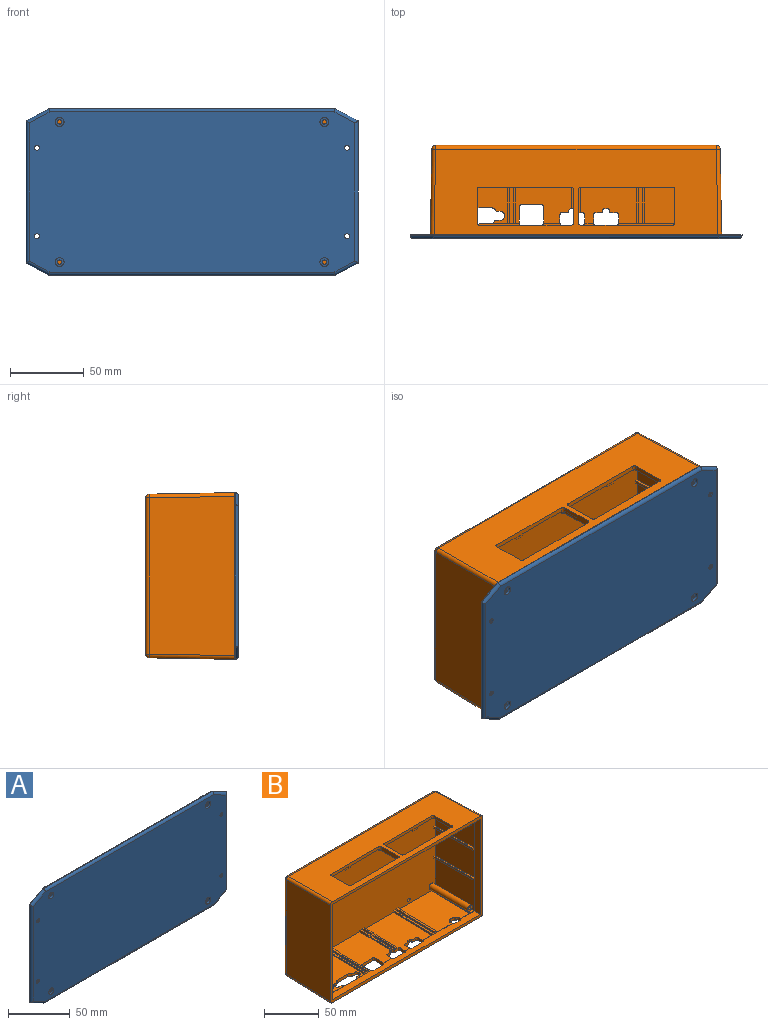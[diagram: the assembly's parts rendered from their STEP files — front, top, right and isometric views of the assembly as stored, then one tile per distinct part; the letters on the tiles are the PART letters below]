
ASSEMBLY  parts=2 mates=1
PART A: 84 faces, bbox 225x7.3x113 mm
  f0: cylinder r=3mm len=6mm, axis (0,-1,0), area 39.6mm2, adj f35,f83
  f1: cylinder r=1.45mm len=3.16mm, axis (0,-1,0), area 28.8mm2, adj f78,f83
  f2: cylinder r=3mm len=6mm, axis (0,-1,0), area 39.6mm2, adj f35,f82
  f3: cylinder r=1.45mm len=3.16mm, axis (0,-1,0), area 28.8mm2, adj f79,f82
  f4: cylinder r=3mm len=6mm, axis (0,-1,0), area 39.6mm2, adj f35,f81
  f5: cylinder r=1.45mm len=3.16mm, axis (0,-1,0), area 28.8mm2, adj f76,f81
  f6: cylinder r=3mm len=6mm, axis (0,-1,0), area 39.6mm2, adj f35,f80
  f7: cylinder r=1.45mm len=3.16mm, axis (0,-1,0), area 28.8mm2, adj f77,f80
  f8: cone r=3.15mm half-angle=45deg, axis (0,1,0), area 31.2mm2, adj f9,f26
  f9: cylinder r=1.7mm len=3.4mm, axis (0,1,0), area 11.6mm2, adj f8,f35
  f10: cone r=3.15mm half-angle=45deg, axis (0,1,0), area 31.2mm2, adj f11,f26
  f11: cylinder r=1.7mm len=3.4mm, axis (0,1,0), area 11.6mm2, adj f10,f35
  f12: cone r=3.15mm half-angle=45deg, axis (0,1,0), area 31.2mm2, adj f13,f26
  f13: cylinder r=1.7mm len=3.4mm, axis (0,1,0), area 11.6mm2, adj f12,f35
  f14: cone r=3.15mm half-angle=45deg, axis (0,1,0), area 31.2mm2, adj f15,f26
  f15: cylinder r=1.7mm len=3.4mm, axis (0,1,0), area 11.6mm2, adj f14,f35
  f16: cylinder r=3.17mm len=6.35mm, axis (0,1,0), area 40.5mm2, adj f44,f79
  f17: cylinder r=3.17mm len=6.35mm, axis (0,1,0), area 40.5mm2, adj f45,f78
  f18: cylinder r=3.17mm len=6.35mm, axis (0,1,0), area 40.5mm2, adj f46,f77
  f19: cylinder r=3.17mm len=6.35mm, axis (0,1,0), area 40.5mm2, adj f47,f76
  f20: cylinder r=0.76mm len=1.52mm, axis (0,-1,0), area 3mm2, adj f26,f67,f69,f70
  f21: cylinder r=0.76mm len=1.52mm, axis (0,-1,0), area 3mm2, adj f26,f58,f60,f61
  f22: cylinder r=4.92mm len=9.84mm, axis (0,-1,0), area 146.9mm2, adj f26,f47
  f23: cylinder r=4.92mm len=9.84mm, axis (0,-1,0), area 146.9mm2, adj f26,f46
  f24: cylinder r=4.92mm len=9.84mm, axis (0,-1,0), area 146.9mm2, adj f26,f45
  f25: cylinder r=4.92mm len=9.84mm, axis (0,-1,0), area 146.9mm2, adj f26,f44
  f26: plane 225.04x113.03mm, normal (0,1,0), area 24179.3mm2, adj f8,f10,f12,f14,f20,f21,f22,f23
  f27: plane 15.75x8.26mm, normal (0.46,0,-0.89), area 5.6mm2, adj f26,f28,f34,f41
  f28: plane 193.55x0.32mm, normal (0,0,-1), area 61.5mm2, adj f26,f27,f29,f43
  f29: plane 15.75x8.26mm, normal (-0.46,0,-0.89), area 5.6mm2, adj f26,f28,f30,f42
  f30: plane 96.52x0.32mm, normal (-1,0,0), area 30.6mm2, adj f26,f29,f31,f40
  f31: plane 15.75x8.26mm, normal (-0.46,0,0.89), area 5.6mm2, adj f26,f30,f32,f38
  f32: plane 193.55x0.32mm, normal (0,0,1), area 61.5mm2, adj f26,f31,f33,f36
  f33: plane 15.75x8.26mm, normal (0.46,0,0.89), area 5.6mm2, adj f26,f32,f34,f37
  f34: plane 96.52x0.32mm, normal (1,0,0), area 30.6mm2, adj f26,f27,f33,f39
  f35: plane 220.6x108.59mm, normal (0,-1,0), area 23596.7mm2, adj f0,f2,f4,f6,f9,f11,f13,f15
  f36: cylinder r=2.22mm len=193.55mm, axis (-1,0,0), area 674.3mm2, adj f32,f35,f37,f38
  f37: cylinder r=2.22mm len=16.78mm, axis (-0.89,0,0.46), area 59.7mm2, adj f33,f35,f36,f39
  f38: cylinder r=2.22mm len=16.78mm, axis (-0.89,0,-0.46), area 59.7mm2, adj f31,f35,f36,f40
  f39: cylinder r=2.22mm len=96.52mm, axis (0,0,1), area 333.5mm2, adj f34,f35,f37,f41
  f40: cylinder r=2.22mm len=96.52mm, axis (0,0,-1), area 333.5mm2, adj f30,f35,f38,f42
  f41: cylinder r=2.22mm len=16.78mm, axis (0.89,0,0.46), area 59.7mm2, adj f27,f35,f39,f43
  f42: cylinder r=2.22mm len=16.78mm, axis (0.89,0,-0.46), area 59.7mm2, adj f29,f35,f40,f43
  f43: cylinder r=2.22mm len=193.55mm, axis (1,0,0), area 674.3mm2, adj f28,f35,f41,f42
  f44: plane 9.84x9.84mm, normal (0,1,0), area 44.4mm2, adj f16,f25
  f45: plane 9.84x9.84mm, normal (0,1,0), area 44.4mm2, adj f17,f24
  f46: plane 9.84x9.84mm, normal (0,1,0), area 44.4mm2, adj f18,f23
  f47: plane 9.84x9.84mm, normal (0,1,0), area 44.4mm2, adj f19,f22
  f48: cylinder r=0.76mm len=1.52mm, axis (0,-1,0), area 3mm2, adj f26,f49,f51,f52
  f49: plane 60.96x1.27mm, normal (0,0,1), area 77.4mm2, adj f26,f48,f50,f52
  f50: cylinder r=0.76mm len=1.52mm, axis (0,-1,0), area 3mm2, adj f26,f49,f51,f52
  f51: plane 60.96x1.27mm, normal (0,0,-1), area 77.4mm2, adj f26,f48,f50,f52
  f52: plane 62.48x1.52mm, normal (0,1,0), area 94.7mm2, adj f48,f49,f50,f51
  f53: cylinder r=0.76mm len=1.52mm, axis (0,-1,0), area 3mm2, adj f26,f54,f56,f57
  f54: plane 60.96x1.27mm, normal (0,0,1), area 77.4mm2, adj f26,f53,f55,f57
  f55: cylinder r=0.76mm len=1.52mm, axis (0,-1,0), area 3mm2, adj f26,f54,f56,f57
  f56: plane 60.96x1.27mm, normal (0,0,-1), area 77.4mm2, adj f26,f53,f55,f57
  f57: plane 62.48x1.52mm, normal (0,1,0), area 94.7mm2, adj f53,f54,f55,f56
  f58: plane 60.96x1.27mm, normal (-1,0,0), area 77.4mm2, adj f21,f26,f59,f61
  f59: cylinder r=0.76mm len=1.52mm, axis (0,-1,0), area 3mm2, adj f26,f58,f60,f61
  f60: plane 60.96x1.27mm, normal (1,0,0), area 77.4mm2, adj f21,f26,f59,f61
  f61: plane 62.48x1.52mm, normal (0,1,0), area 94.7mm2, adj f21,f58,f59,f60
  f62: cylinder r=0.76mm len=1.52mm, axis (0,-1,0), area 3mm2, adj f26,f63,f65,f66
  f63: plane 60.96x1.27mm, normal (0,0,-1), area 77.4mm2, adj f26,f62,f64,f66
  f64: cylinder r=0.76mm len=1.52mm, axis (0,-1,0), area 3mm2, adj f26,f63,f65,f66
  f65: plane 60.96x1.27mm, normal (0,0,1), area 77.4mm2, adj f26,f62,f64,f66
  f66: plane 62.48x1.52mm, normal (0,1,0), area 94.7mm2, adj f62,f63,f64,f65
  f67: plane 60.96x1.27mm, normal (-1,0,0), area 77.4mm2, adj f20,f26,f68,f70
  f68: cylinder r=0.76mm len=1.52mm, axis (0,-1,0), area 3mm2, adj f26,f67,f69,f70
  f69: plane 60.96x1.27mm, normal (1,0,0), area 77.4mm2, adj f20,f26,f68,f70
  f70: plane 62.48x1.52mm, normal (0,1,0), area 94.7mm2, adj f20,f67,f68,f69
  f71: cylinder r=0.76mm len=1.52mm, axis (0,-1,0), area 3mm2, adj f26,f72,f74,f75
  f72: plane 60.96x1.27mm, normal (0,0,-1), area 77.4mm2, adj f26,f71,f73,f75
  f73: cylinder r=0.76mm len=1.52mm, axis (0,-1,0), area 3mm2, adj f26,f72,f74,f75
  f74: plane 60.96x1.27mm, normal (0,0,1), area 77.4mm2, adj f26,f71,f73,f75
  f75: plane 62.48x1.52mm, normal (0,1,0), area 94.7mm2, adj f71,f72,f73,f74
  f76: plane 6.35x6.35mm, normal (0,1,0), area 25.1mm2, adj f5,f19
  f77: plane 6.35x6.35mm, normal (0,1,0), area 25.1mm2, adj f7,f18
  f78: plane 6.35x6.35mm, normal (0,1,0), area 25.1mm2, adj f1,f17
  f79: plane 6.35x6.35mm, normal (0,1,0), area 25.1mm2, adj f3,f16
  f80: plane 6x6mm, normal (0,-1,0), area 21.7mm2, adj f6,f7
  f81: plane 6x6mm, normal (0,-1,0), area 21.7mm2, adj f4,f5
  f82: plane 6x6mm, normal (0,-1,0), area 21.7mm2, adj f2,f3
  f83: plane 6x6mm, normal (0,-1,0), area 21.7mm2, adj f0,f1
PART B: 273 faces, bbox 197.4x60.5x113 mm
  f0: cylinder r=1.65mm len=3.3mm, axis (0,1,0), area 32.9mm2, adj f96,f111
  f1: cylinder r=1.38mm len=49.53mm, axis (0,1,0), area 430.8mm2, adj f193,f197
  f2: cylinder r=1.38mm len=49.53mm, axis (0,1,0), area 430.8mm2, adj f193,f196
  f3: cylinder r=1.38mm len=49.53mm, axis (0,1,0), area 430.8mm2, adj f192,f195
  f4: cylinder r=1.38mm len=49.53mm, axis (0,1,0), area 430.8mm2, adj f192,f194
  f5: cylinder r=3.17mm len=6.35mm, axis (0,0,1), area 31.7mm2, adj f18,f59,f184,f185
  f6: torus R=2.09mm, axis (0,-1,0), area 5.6mm2, adj f111,f112
  f7: torus R=2.09mm, axis (0,-1,0), area 6.5mm2, adj f96,f110
  f8: cylinder r=3.17mm len=49.53mm, axis (0,1,0), area 956.6mm2, adj f84,f85,f111,f149,f192
  f9: cylinder r=3.17mm len=49.53mm, axis (0,1,0), area 956.6mm2, adj f86,f87,f111,f150,f193
  f10: cylinder r=3.17mm len=49.53mm, axis (0,1,0), area 956.6mm2, adj f80,f81,f111,f117,f192
  f11: cylinder r=3.17mm len=49.53mm, axis (0,1,0), area 956.6mm2, adj f82,f83,f111,f118,f193
  f12: plane 49.53x5.33mm, normal (0,-0.02,1), area 242.4mm2, adj f39,f86,f111,f193
  f13: plane 49.53x42.76mm, normal (0,-0.02,1), area 2062.1mm2, adj f34,f87,f111,f193,f230,f231,f233,f234
  f14: plane 49.53x2.16mm, normal (0,-0.02,1), area 107mm2, adj f33,f37,f111,f269
  f15: plane 49.53x37.72mm, normal (0,-0.02,1), area 1712mm2, adj f36,f93,f111,f226,f229,f238,f239,f241
  f16: plane 49.53x37.72mm, normal (0,-0.02,1), area 1596.8mm2, adj f28,f91,f111,f199,f200,f201,f218,f219
  f17: plane 49.53x2.16mm, normal (0,-0.02,1), area 107mm2, adj f27,f31,f111,f270
  f18: plane 49.53x42.76mm, normal (0,-0.02,1), area 1855.7mm2, adj f5,f30,f84,f111,f181,f182,f183,f184
  f19: plane 49.53x5.33mm, normal (0,-0.02,1), area 242.4mm2, adj f42,f85,f111,f192
  f20: plane 49.53x5.33mm, normal (0,-0.02,-1), area 242.4mm2, adj f41,f82,f111,f193
  f21: plane 49.53x42.76mm, normal (0,-0.02,-1), area 1625.2mm2, adj f75,f83,f111,f193,f202,f203,f215,f216
  f22: plane 49.53x2.16mm, normal (0,-0.02,-1), area 107mm2, adj f57,f58,f111,f266
  f23: plane 49.53x42.76mm, normal (0,-0.02,-1), area 1625.2mm2, adj f73,f80,f111,f192,f206,f209,f212,f213
  f24: plane 49.53x5.33mm, normal (0,-0.02,-1), area 242.4mm2, adj f44,f81,f111,f192
  f25: plane 33.87x1.91mm, normal (0,-0.02,-1), area 34.6mm2, adj f57,f70,f145,f207,f210,f211,f266
  f26: plane 33.87x1.91mm, normal (0,-0.02,-1), area 34.6mm2, adj f58,f79,f146,f204,f214,f217,f266
  f27: plane 49.53x2.85mm, normal (-1,0,0), area 81.6mm2, adj f17,f29,f152,f159,f160,f173,f175,f270
  f28: plane 49.53x2.85mm, normal (1,0,0), area 81.6mm2, adj f16,f29,f152,f159,f160,f173,f175,f270
  f29: plane 33.87x1.91mm, normal (0,-0.02,1), area 64.5mm2, adj f27,f28,f175,f270
  f30: plane 49.53x2.85mm, normal (-1,0,0), area 81.6mm2, adj f18,f32,f153,f157,f158,f174,f176,f270
  f31: plane 49.53x2.85mm, normal (1,0,0), area 81.6mm2, adj f17,f32,f153,f157,f158,f174,f176,f270
  f32: plane 33.87x1.91mm, normal (0,-0.02,1), area 64.5mm2, adj f30,f31,f176,f270
  f33: plane 49.53x2.85mm, normal (-1,0,0), area 81.6mm2, adj f14,f35,f154,f167,f168,f169,f180,f269
  f34: plane 49.53x2.85mm, normal (1,0,0), area 81.6mm2, adj f13,f35,f154,f167,f168,f169,f180,f269
  f35: plane 33.87x1.91mm, normal (0,-0.02,1), area 64.5mm2, adj f33,f34,f180,f269
  f36: plane 49.53x2.85mm, normal (-1,0,0), area 81.6mm2, adj f15,f38,f155,f165,f166,f170,f179,f269
  f37: plane 49.53x2.85mm, normal (1,0,0), area 81.6mm2, adj f14,f38,f155,f165,f166,f170,f179,f269
  f38: plane 33.87x1.91mm, normal (0,-0.02,1), area 64.5mm2, adj f36,f37,f179,f269
  f39: plane 49.53x35.58mm, normal (-1,-0.02,0), area 1740.9mm2, adj f12,f51,f111,f193
  f40: plane 49.53x31.42mm, normal (-1,-0.02,0), area 1556.5mm2, adj f52,f54,f111,f193
  f41: plane 49.53x35.58mm, normal (-1,-0.02,0), area 1740.9mm2, adj f20,f55,f111,f193
  f42: plane 49.53x35.58mm, normal (1,-0.02,0), area 1740.9mm2, adj f19,f46,f111,f192
  f43: plane 49.53x31.42mm, normal (1,-0.02,0), area 1556.5mm2, adj f45,f49,f111,f192
  f44: plane 49.53x35.58mm, normal (1,-0.02,0), area 1740.9mm2, adj f24,f48,f111,f192
  f45: plane 49.53x2.45mm, normal (0,0,1), area 78.6mm2, adj f43,f47,f113,f192
  f46: plane 49.53x2.45mm, normal (0,0,-1), area 78.6mm2, adj f42,f47,f113,f192
  f47: plane 49.5x1.91mm, normal (1,-0.02,0), area 94.3mm2, adj f45,f46,f113,f192
  f48: plane 49.53x2.45mm, normal (0,0,1), area 78.6mm2, adj f44,f50,f114,f192
  f49: plane 49.53x2.45mm, normal (0,0,-1), area 78.6mm2, adj f43,f50,f114,f192
  f50: plane 49.5x1.91mm, normal (1,-0.02,0), area 94.3mm2, adj f48,f49,f114,f192
  f51: plane 49.53x2.45mm, normal (0,0,-1), area 78.6mm2, adj f39,f53,f115,f193
  f52: plane 49.53x2.45mm, normal (0,0,1), area 78.6mm2, adj f40,f53,f115,f193
  f53: plane 49.5x1.91mm, normal (-1,-0.02,0), area 94.3mm2, adj f51,f52,f115,f193
  f54: plane 49.53x2.45mm, normal (0,0,-1), area 78.6mm2, adj f40,f56,f116,f193
  f55: plane 49.53x2.45mm, normal (0,0,1), area 78.6mm2, adj f41,f56,f116,f193
  f56: plane 49.5x1.91mm, normal (-1,-0.02,0), area 94.3mm2, adj f54,f55,f116,f193
  f57: plane 49.53x2.85mm, normal (1,0,0), area 81.6mm2, adj f22,f25,f119,f129,f130,f140,f145,f266
  f58: plane 49.53x2.85mm, normal (-1,0,0), area 81.6mm2, adj f22,f26,f124,f131,f132,f139,f146,f266
  f59: plane 192.33x57.98mm, normal (0,0.02,-1), area 10210.2mm2, adj f5,f97,f99,f105,f106,f181,f182,f183
  f60: plane 42.14x2.16mm, normal (0,-0.02,1), area 88.8mm2, adj f90,f92,f111,f225,f229,f248
  f61: plane 9.38x1.91mm, normal (0,-0.02,-1), area 17.9mm2, adj f75,f76,f148,f203
  f62: plane 9.38x1.91mm, normal (0,-0.02,-1), area 17.9mm2, adj f77,f78,f147,f203
  f63: plane 9.38x1.91mm, normal (0,-0.02,-1), area 17.9mm2, adj f71,f72,f143,f209
  f64: plane 9.38x1.91mm, normal (0,-0.02,-1), area 17.9mm2, adj f73,f74,f144,f209
  f65: plane 25.04x2.16mm, normal (0,-0.02,-1), area 54.1mm2, adj f76,f77,f111,f203
  f66: plane 37.72x25.08mm, normal (0,-0.02,-1), area 944.8mm2, adj f78,f79,f111,f203,f217
  f67: plane 37.72x25.08mm, normal (0,-0.02,-1), area 944.8mm2, adj f70,f72,f111,f209,f211
  f68: plane 25.04x2.16mm, normal (0,-0.02,-1), area 54.1mm2, adj f71,f74,f111,f209
  f69: plane 192.33x57.98mm, normal (0,0.02,1), area 7725.8mm2, adj f97,f98,f103,f104,f202,f203,f204,f205
  f70: plane 25.08x2.42mm, normal (-1,0,0), area 42.7mm2, adj f25,f67,f119,f129,f130,f140,f145,f211
  f71: plane 25.04x2.42mm, normal (-1,0,0), area 42.7mm2, adj f63,f68,f120,f127,f128,f141,f143,f209
  f72: plane 25.04x2.42mm, normal (1,0,0), area 42.7mm2, adj f63,f67,f120,f127,f128,f141,f143,f209
  f73: plane 25.04x2.42mm, normal (-1,0,0), area 42.7mm2, adj f23,f64,f121,f125,f126,f142,f144,f209
  f74: plane 25.04x2.42mm, normal (1,0,0), area 42.7mm2, adj f64,f68,f121,f125,f126,f142,f144,f209
  f75: plane 25.04x2.42mm, normal (1,0,0), area 42.7mm2, adj f21,f61,f122,f135,f136,f137,f148,f203
  f76: plane 25.04x2.42mm, normal (-1,0,0), area 42.7mm2, adj f61,f65,f122,f135,f136,f137,f148,f203
  f77: plane 25.04x2.42mm, normal (1,0,0), area 42.7mm2, adj f62,f65,f123,f133,f134,f138,f147,f203
  f78: plane 25.04x2.42mm, normal (-1,0,0), area 42.7mm2, adj f62,f66,f123,f133,f134,f138,f147,f203
  f79: plane 25.08x2.42mm, normal (1,0,0), area 42.7mm2, adj f26,f66,f124,f131,f132,f139,f146,f217
  f80: plane 49.53x2.53mm, normal (1,0,0), area 104.1mm2, adj f10,f23,f117,f192
  f81: plane 49.53x2.53mm, normal (-1,0,0), area 104.1mm2, adj f10,f24,f117,f192
  f82: plane 49.53x2.53mm, normal (1,0,0), area 104.1mm2, adj f11,f20,f118,f193
  f83: plane 49.53x2.53mm, normal (-1,0,0), area 104.1mm2, adj f11,f21,f118,f193
  f84: plane 49.53x2.53mm, normal (1,0,0), area 104.1mm2, adj f8,f18,f149,f192
  f85: plane 49.53x2.53mm, normal (-1,0,0), area 104.1mm2, adj f8,f19,f149,f192
  f86: plane 49.53x2.53mm, normal (1,0,0), area 104.1mm2, adj f9,f12,f150,f193
  f87: plane 49.53x2.53mm, normal (-1,0,0), area 104.1mm2, adj f9,f13,f150,f193
  f88: plane 26.48x1.91mm, normal (0,-0.02,1), area 50.4mm2, adj f92,f93,f178,f229
  f89: plane 24x1.91mm, normal (0,-0.02,1), area 45.6mm2, adj f90,f91,f177,f227,f248
  f90: plane 39.66x2.68mm, normal (1,0,0), area 65.9mm2, adj f60,f89,f151,f161,f162,f172,f177,f248
  f91: plane 39.57x2.67mm, normal (-1,0,0), area 65.7mm2, adj f16,f89,f151,f161,f162,f172,f177,f227
  f92: plane 42.14x2.72mm, normal (-1,0,0), area 69.8mm2, adj f60,f88,f156,f163,f164,f171,f178,f229
  f93: plane 42.14x2.72mm, normal (1,0,0), area 69.8mm2, adj f15,f88,f156,f163,f164,f171,f178,f229
  f94: plane 107.93x57.98mm, normal (1,0.02,0), area 6200mm2, adj f97,f98,f99,f100
  f95: plane 107.93x57.98mm, normal (-1,0.02,0), area 6200mm2, adj f97,f104,f105,f109
  f96: plane 190.31x105.9mm, normal (0,1,0), area 20119.4mm2, adj f0,f7,f100,f103,f106,f109
  f97: plane 197.41x113mm, normal (0,-1,0), area 1925.6mm2, adj f59,f69,f94,f95,f98,f99,f104,f105
  f98: cylinder r=2.54mm len=58.02mm, axis (0.02,-1,0.02), area 231.4mm2, adj f69,f94,f97,f101
  f99: cylinder r=2.54mm len=58.02mm, axis (0.02,-1,-0.02), area 231.4mm2, adj f59,f94,f97,f102
  f100: cylinder r=2.54mm len=105.9mm, axis (0,0,-1), area 417.8mm2, adj f94,f96,f101,f102
  f101: sphere r=2.54mm, area 9.9mm2, adj f98,f100,f103
  f102: sphere r=2.54mm, area 9.9mm2, adj f99,f100,f106
  f103: cylinder r=2.54mm len=190.31mm, axis (1,0,0), area 750.8mm2, adj f69,f96,f101,f107
  f104: cylinder r=2.54mm len=58.02mm, axis (-0.02,-1,0.02), area 231.4mm2, adj f69,f95,f97,f107
  f105: cylinder r=2.54mm len=58.02mm, axis (-0.02,-1,-0.02), area 231.4mm2, adj f59,f95,f97,f108
  f106: cylinder r=2.54mm len=190.31mm, axis (1,0,0), area 750.8mm2, adj f59,f96,f102,f108
  f107: sphere r=2.54mm, area 9.9mm2, adj f103,f104,f109
  f108: sphere r=2.54mm, area 9.9mm2, adj f105,f106,f109
  f109: cylinder r=2.54mm len=105.9mm, axis (0,0,-1), area 417.8mm2, adj f95,f96,f107,f108
  f110: sphere r=16.2mm, area 19.4mm2, adj f7
  f111: plane 189.06x104.65mm, normal (0,-1,0), area 19617.1mm2, adj f0,f6,f8,f9,f10,f11,f12,f13
  f112: sphere r=19.38mm, area 27.8mm2, adj f6
  f113: plane 1.91x1.59mm, normal (0.02,1,0), area 3mm2, adj f45,f46,f47,f111
  f114: plane 1.91x1.59mm, normal (0.02,1,0), area 3mm2, adj f48,f49,f50,f111
  f115: plane 1.91x1.59mm, normal (-0.02,1,0), area 3mm2, adj f51,f52,f53,f111
  f116: plane 1.91x1.59mm, normal (-0.02,1,0), area 3mm2, adj f54,f55,f56,f111
  f117: plane 1.67x0.64mm, normal (0,1,-0.02), area 1.1mm2, adj f10,f80,f81,f111
  f118: plane 1.67x0.64mm, normal (0,1,-0.02), area 1.1mm2, adj f11,f82,f83,f111
  f119: plane 1.98x1.91mm, normal (0,1,-0.02), area 3.8mm2, adj f57,f70,f111,f130
  f120: plane 1.98x1.91mm, normal (0,1,-0.02), area 3.8mm2, adj f71,f72,f111,f128
  f121: plane 1.98x1.91mm, normal (0,1,-0.02), area 3.8mm2, adj f73,f74,f111,f126
  f122: plane 1.98x1.91mm, normal (0,1,-0.02), area 3.8mm2, adj f75,f76,f111,f136
  f123: plane 1.98x1.91mm, normal (0,1,-0.02), area 3.8mm2, adj f77,f78,f111,f134
  f124: plane 1.98x1.91mm, normal (0,1,-0.02), area 3.8mm2, adj f58,f79,f111,f132
  f125: plane 1.91x0.79mm, normal (0,-1,0.02), area 1.5mm2, adj f73,f74,f126,f142
  f126: plane 11.43x1.91mm, normal (0,-0.02,-1), area 21.8mm2, adj f73,f74,f121,f125
  f127: plane 1.91x0.79mm, normal (0,-1,0.02), area 1.5mm2, adj f71,f72,f128,f141
  f128: plane 11.43x1.91mm, normal (0,-0.02,-1), area 21.8mm2, adj f71,f72,f120,f127
  f129: plane 1.91x0.79mm, normal (0,-1,0.02), area 1.5mm2, adj f57,f70,f130,f140
  f130: plane 11.43x1.91mm, normal (0,-0.02,-1), area 21.8mm2, adj f57,f70,f119,f129
  f131: plane 1.91x0.79mm, normal (0,-1,0.02), area 1.5mm2, adj f58,f79,f132,f139
  f132: plane 11.43x1.91mm, normal (0,-0.02,-1), area 21.8mm2, adj f58,f79,f124,f131
  f133: plane 1.91x0.79mm, normal (0,-1,0.02), area 1.5mm2, adj f77,f78,f134,f138
  f134: plane 11.43x1.91mm, normal (0,-0.02,-1), area 21.8mm2, adj f77,f78,f123,f133
  f135: plane 1.91x0.79mm, normal (0,-1,0.02), area 1.5mm2, adj f75,f76,f136,f137
  f136: plane 11.43x1.91mm, normal (0,-0.02,-1), area 21.8mm2, adj f75,f76,f122,f135
  f137: plane 3.81x1.91mm, normal (0,-0.02,-1), area 7.3mm2, adj f75,f76,f135,f148
  f138: plane 3.81x1.91mm, normal (0,-0.02,-1), area 7.3mm2, adj f77,f78,f133,f147
  f139: plane 3.81x1.91mm, normal (0,-0.02,-1), area 7.3mm2, adj f58,f79,f131,f146
  f140: plane 3.81x1.91mm, normal (0,-0.02,-1), area 7.3mm2, adj f57,f70,f129,f145
  f141: plane 3.81x1.91mm, normal (0,-0.02,-1), area 7.3mm2, adj f71,f72,f127,f143
  f142: plane 3.81x1.91mm, normal (0,-0.02,-1), area 7.3mm2, adj f73,f74,f125,f144
  f143: plane 1.91x0.4mm, normal (0,0.69,-0.72), area 1.1mm2, adj f63,f71,f72,f141
  f144: plane 1.91x0.4mm, normal (0,0.69,-0.72), area 1.1mm2, adj f64,f73,f74,f142
  f145: plane 1.91x0.4mm, normal (0,0.69,-0.72), area 1.1mm2, adj f25,f57,f70,f140
  f146: plane 1.91x0.4mm, normal (0,0.69,-0.72), area 1.1mm2, adj f26,f58,f79,f139
  f147: plane 1.91x0.4mm, normal (0,0.69,-0.72), area 1.1mm2, adj f62,f77,f78,f138
  f148: plane 1.91x0.4mm, normal (0,0.69,-0.72), area 1.1mm2, adj f61,f75,f76,f137
  f149: plane 1.67x0.64mm, normal (0,1,0.02), area 1.1mm2, adj f8,f84,f85,f111
  f150: plane 1.67x0.64mm, normal (0,1,0.02), area 1.1mm2, adj f9,f86,f87,f111
  f151: plane 1.98x1.91mm, normal (0,1,0.02), area 3.8mm2, adj f90,f91,f111,f162
  f152: plane 1.98x1.91mm, normal (0,1,0.02), area 3.8mm2, adj f27,f28,f111,f160
  f153: plane 1.98x1.91mm, normal (0,1,0.02), area 3.8mm2, adj f30,f31,f111,f158
  f154: plane 1.98x1.91mm, normal (0,1,0.02), area 3.8mm2, adj f33,f34,f111,f168
  f155: plane 1.98x1.91mm, normal (0,1,0.02), area 3.8mm2, adj f36,f37,f111,f166
  f156: plane 1.98x1.91mm, normal (0,1,0.02), area 3.8mm2, adj f92,f93,f111,f164
  f157: plane 1.91x0.79mm, normal (0,-1,-0.02), area 1.5mm2, adj f30,f31,f158,f174
  f158: plane 11.43x1.91mm, normal (0,-0.02,1), area 21.8mm2, adj f30,f31,f153,f157
  f159: plane 1.91x0.79mm, normal (0,-1,-0.02), area 1.5mm2, adj f27,f28,f160,f173
  f160: plane 11.43x1.91mm, normal (0,-0.02,1), area 21.8mm2, adj f27,f28,f152,f159
  f161: plane 1.91x0.79mm, normal (0,-1,-0.02), area 1.5mm2, adj f90,f91,f162,f172
  f162: plane 11.43x1.91mm, normal (0,-0.02,1), area 21.8mm2, adj f90,f91,f151,f161
  f163: plane 1.91x0.79mm, normal (0,-1,-0.02), area 1.5mm2, adj f92,f93,f164,f171
  f164: plane 11.43x1.91mm, normal (0,-0.02,1), area 21.8mm2, adj f92,f93,f156,f163
  f165: plane 1.91x0.79mm, normal (0,-1,-0.02), area 1.5mm2, adj f36,f37,f166,f170
  f166: plane 11.43x1.91mm, normal (0,-0.02,1), area 21.8mm2, adj f36,f37,f155,f165
  f167: plane 1.91x0.79mm, normal (0,-1,-0.02), area 1.5mm2, adj f33,f34,f168,f169
  f168: plane 11.43x1.91mm, normal (0,-0.02,1), area 21.8mm2, adj f33,f34,f154,f167
  f169: plane 3.81x1.91mm, normal (0,-0.02,1), area 7.3mm2, adj f33,f34,f167,f180
  f170: plane 3.81x1.91mm, normal (0,-0.02,1), area 7.3mm2, adj f36,f37,f165,f179
  f171: plane 3.81x1.91mm, normal (0,-0.02,1), area 7.3mm2, adj f92,f93,f163,f178
  f172: plane 3.81x1.91mm, normal (0,-0.02,1), area 7.3mm2, adj f90,f91,f161,f177
  f173: plane 3.81x1.91mm, normal (0,-0.02,1), area 7.3mm2, adj f27,f28,f159,f175
  f174: plane 3.81x1.91mm, normal (0,-0.02,1), area 7.3mm2, adj f30,f31,f157,f176
  f175: plane 1.91x0.4mm, normal (0,0.69,0.72), area 1.1mm2, adj f27,f28,f29,f173
  f176: plane 1.91x0.4mm, normal (0,0.69,0.72), area 1.1mm2, adj f30,f31,f32,f174
  f177: plane 1.91x0.4mm, normal (0,0.69,0.72), area 1.1mm2, adj f89,f90,f91,f172
  f178: plane 1.91x0.4mm, normal (0,0.69,0.72), area 1.1mm2, adj f88,f92,f93,f171
  f179: plane 1.91x0.4mm, normal (0,0.69,0.72), area 1.1mm2, adj f36,f37,f38,f170
  f180: plane 1.91x0.4mm, normal (0,0.69,0.72), area 1.1mm2, adj f33,f34,f35,f169
  f181: cylinder r=3.35mm len=3.21mm, axis (0,0,1), area 12.8mm2, adj f18,f59,f182,f191
  f182: plane 13.41x3.18mm, normal (0,-1,0), area 42.6mm2, adj f18,f59,f181,f183
  f183: cylinder r=3.35mm len=3.21mm, axis (0,0,1), area 12.8mm2, adj f18,f59,f182,f184
  f184: plane 3.18x2.63mm, normal (0,-1,0), area 8.4mm2, adj f5,f18,f59,f183
  f185: plane 3.33x3.18mm, normal (0,1,0), area 10.6mm2, adj f5,f18,f59,f186
  f186: cylinder r=3.35mm len=3.21mm, axis (0,0,1), area 12.7mm2, adj f18,f59,f185,f187,f265,f270
  f187: plane 12.01x3.04mm, normal (0,1,0), area 36.6mm2, adj f59,f186,f188,f265
  f188: cylinder r=3.35mm len=3.21mm, axis (0,0,1), area 12.7mm2, adj f18,f59,f187,f189,f192,f265
  f189: plane 3.33x3.18mm, normal (0,1,0), area 10.6mm2, adj f18,f59,f188,f190
  f190: cylinder r=3.17mm len=6.35mm, axis (0,0,1), area 31.7mm2, adj f18,f59,f189,f191
  f191: plane 3.18x2.63mm, normal (0,-1,0), area 8.4mm2, adj f18,f59,f181,f190
  f192: plane 106.65x28.71mm, normal (0,-1,0), area 82.2mm2, adj f3,f4,f8,f10,f18,f19,f23,f24
  f193: plane 106.65x28.71mm, normal (0,-1,0), area 81.3mm2, adj f1,f2,f9,f11,f12,f13,f20,f21
  f194: plane 2.77x2.77mm, normal (0,-1,0), area 6mm2, adj f4
  f195: plane 2.77x2.77mm, normal (0,-1,0), area 6mm2, adj f3
  f196: plane 2.77x2.77mm, normal (0,-1,0), area 6mm2, adj f2
  f197: plane 2.77x2.77mm, normal (0,-1,0), area 6mm2, adj f1
  f198: plane 13.59x3.06mm, normal (0,1,0), area 41.6mm2, adj f59,f220,f221,f265
  f199: plane 10.8x3.36mm, normal (1,0,0), area 34.3mm2, adj f16,f59,f219,f220
  f200: plane 13.59x3.18mm, normal (0,-1,0), area 43.2mm2, adj f16,f59,f218,f219
  f201: plane 10.8x3.36mm, normal (-1,0,0), area 34.3mm2, adj f16,f59,f218,f221
  f202: plane 22.73x3.57mm, normal (-1,0,0), area 72.2mm2, adj f21,f69,f215,f216
  f203: plane 61.91x4.76mm, normal (0,-1,0), area 202.7mm2, adj f21,f61,f62,f65,f66,f69,f75,f76
  f204: plane 22.73x5.16mm, normal (1,0,0), area 108.3mm2, adj f26,f69,f214,f217
  f205: plane 61.91x3.06mm, normal (0,1,0), area 189.7mm2, adj f69,f214,f215,f264
  f206: plane 22.73x3.57mm, normal (1,0,0), area 72.2mm2, adj f23,f69,f212,f213
  f207: plane 22.73x5.16mm, normal (-1,0,0), area 108.3mm2, adj f25,f69,f210,f211
  f208: plane 61.91x3.06mm, normal (0,1,0), area 189.7mm2, adj f69,f210,f212,f264
  f209: plane 61.91x4.76mm, normal (0,-1,0), area 202.7mm2, adj f23,f63,f64,f67,f68,f69,f71,f72
  f210: cylinder r=1.59mm len=4.79mm, axis (0,0,1), area 7.9mm2, adj f25,f69,f207,f208,f264,f266
  f211: cylinder r=1.59mm len=4.79mm, axis (0,0,1), area 11.3mm2, adj f25,f67,f69,f70,f207,f209
  f212: cylinder r=1.59mm len=3.2mm, axis (0,0,1), area 7.6mm2, adj f23,f69,f192,f206,f208,f264
  f213: cylinder r=1.59mm len=3.2mm, axis (0,0,1), area 7.9mm2, adj f23,f69,f206,f209
  f214: cylinder r=1.59mm len=4.79mm, axis (0,0,1), area 7.9mm2, adj f26,f69,f204,f205,f264,f266
  f215: cylinder r=1.59mm len=3.2mm, axis (0,0,1), area 7.6mm2, adj f21,f69,f193,f202,f205,f264
  f216: cylinder r=1.59mm len=3.2mm, axis (0,0,1), area 7.9mm2, adj f21,f69,f202,f203
  f217: cylinder r=1.59mm len=4.79mm, axis (0,0,1), area 11.3mm2, adj f26,f66,f69,f79,f203,f204
  f218: cylinder r=1.59mm len=3.2mm, axis (0,0,-1), area 7.9mm2, adj f16,f59,f200,f201
  f219: cylinder r=1.59mm len=3.2mm, axis (0,0,-1), area 7.9mm2, adj f16,f59,f199,f200
  f220: cylinder r=1.59mm len=3.2mm, axis (0,0,-1), area 7.6mm2, adj f16,f59,f198,f199,f265,f270
  f221: cylinder r=1.59mm len=3.2mm, axis (0,0,-1), area 7.6mm2, adj f16,f59,f198,f201,f265,f267
  f222: plane 5.67x3.27mm, normal (1,0,0), area 18mm2, adj f16,f59,f246,f250
  f223: plane 4.41x3.18mm, normal (0,-1,0), area 14mm2, adj f16,f59,f224,f246
  f224: plane 3.19x0.98mm, normal (1,0,0), area 3.1mm2, adj f16,f59,f223,f247
  f225: plane 3.19x0.98mm, normal (-1,0,0), area 3.1mm2, adj f59,f60,f229,f248
  f226: plane 5.67x3.27mm, normal (-1,0,0), area 18mm2, adj f15,f59,f249,f251
  f227: plane 4.76x1.7mm, normal (0,-1,0), area 7.6mm2, adj f16,f59,f89,f91,f247,f248
  f228: plane 13.69x3.07mm, normal (0,1,0), area 42mm2, adj f59,f250,f251,f265
  f229: plane 4.76x4.4mm, normal (0,-1,0), area 17mm2, adj f15,f59,f60,f88,f92,f93,f225,f249
  f230: plane 3.18x0.8mm, normal (0,-1,0), area 2.5mm2, adj f13,f59,f237,f258
  f231: plane 3.22x2.63mm, normal (-1,0,0), area 8.4mm2, adj f13,f59,f258,f263
  f232: plane 7.69x3.07mm, normal (0,1,0), area 23.6mm2, adj f59,f259,f263,f265
  f233: plane 3.22x2.63mm, normal (1,0,0), area 8.4mm2, adj f13,f59,f259,f260
  f234: plane 3.18x0.79mm, normal (0,-1,0), area 2.5mm2, adj f13,f59,f235,f260
  f235: plane 3.18x0.21mm, normal (1,0,0), area 0.7mm2, adj f13,f59,f234,f261
  f236: plane 3.18x2.93mm, normal (0,-1,0), area 9.3mm2, adj f13,f59,f261,f262
  f237: plane 3.18x0.21mm, normal (-1,0,0), area 0.7mm2, adj f13,f59,f230,f262
  f238: plane 4.4x3.18mm, normal (0,-1,0), area 14mm2, adj f15,f59,f245,f252
  f239: plane 5.67x3.27mm, normal (-1,0,0), area 18mm2, adj f15,f59,f252,f257
  f240: plane 13.69x3.07mm, normal (0,1,0), area 42mm2, adj f59,f253,f257,f265
  f241: plane 5.67x3.27mm, normal (1,0,0), area 18mm2, adj f15,f59,f253,f254
  f242: plane 4.41x3.18mm, normal (0,-1,0), area 14mm2, adj f15,f59,f243,f254
  f243: plane 3.19x0.98mm, normal (1,0,0), area 3.1mm2, adj f15,f59,f242,f255
  f244: plane 3.18x1.7mm, normal (0,-1,0), area 5.4mm2, adj f15,f59,f255,f256
  f245: plane 3.19x0.98mm, normal (-1,0,0), area 3.1mm2, adj f15,f59,f238,f256
  f246: cylinder r=1.59mm len=3.2mm, axis (0,0,-1), area 7.9mm2, adj f16,f59,f222,f223
  f247: cylinder r=1.59mm len=3.2mm, axis (0,0,-1), area 7.9mm2, adj f16,f59,f224,f227
  f248: cylinder r=1.59mm len=4.79mm, axis (0,0,-1), area 8.8mm2, adj f59,f60,f89,f90,f225,f227
  f249: cylinder r=1.59mm len=3.2mm, axis (0,0,-1), area 7.9mm2, adj f15,f59,f226,f229
  f250: cylinder r=1.59mm len=3.2mm, axis (0,0,1), area 7.6mm2, adj f16,f59,f222,f228,f265,f267
  f251: cylinder r=1.59mm len=3.2mm, axis (0,0,1), area 7.6mm2, adj f15,f59,f226,f228,f265,f268
  f252: cylinder r=1.59mm len=3.2mm, axis (0,0,-1), area 7.9mm2, adj f15,f59,f238,f239
  f253: cylinder r=1.59mm len=3.2mm, axis (0,0,1), area 7.6mm2, adj f15,f59,f240,f241,f265,f268
  f254: cylinder r=1.59mm len=3.2mm, axis (0,0,-1), area 7.9mm2, adj f15,f59,f241,f242
  f255: cylinder r=1.59mm len=3.2mm, axis (0,0,-1), area 7.9mm2, adj f15,f59,f243,f244
  f256: cylinder r=1.59mm len=3.2mm, axis (0,0,-1), area 7.9mm2, adj f15,f59,f244,f245
  f257: cylinder r=1.59mm len=3.2mm, axis (0,0,1), area 7.6mm2, adj f15,f59,f239,f240,f265,f269
  f258: cylinder r=1.59mm len=3.2mm, axis (0,0,-1), area 7.9mm2, adj f13,f59,f230,f231
  f259: cylinder r=1.59mm len=3.2mm, axis (0,0,1), area 7.6mm2, adj f13,f59,f232,f233,f265,f269
  f260: cylinder r=1.59mm len=3.2mm, axis (0,0,-1), area 7.9mm2, adj f13,f59,f233,f234
  f261: cylinder r=1.59mm len=3.2mm, axis (0,0,-1), area 7.9mm2, adj f13,f59,f235,f236
  f262: cylinder r=1.59mm len=3.2mm, axis (0,0,-1), area 7.9mm2, adj f13,f59,f236,f237
  f263: cylinder r=1.59mm len=3.2mm, axis (0,0,1), area 7.6mm2, adj f13,f59,f193,f231,f232,f265
  f264: plane 191.06x7.77mm, normal (0,0,-1), area 1302mm2, adj f97,f192,f193,f205,f208,f210,f212,f214
  f265: plane 191.06x7.77mm, normal (0,0,1), area 1398.6mm2, adj f97,f186,f187,f188,f192,f193,f198,f220
  f266: plane 3.5x1.72mm, normal (0,-1,0), area 2.6mm2, adj f22,f25,f26,f57,f58,f210,f214,f264
  f267: plane 10.93x0.14mm, normal (0,-1,0), area 1.5mm2, adj f16,f221,f250,f265
  f268: plane 6.01x0.14mm, normal (0,-1,0), area 0.8mm2, adj f15,f251,f253,f265
  f269: plane 38.15x1.72mm, normal (0,-1,0), area 11.2mm2, adj f13,f14,f15,f33,f34,f35,f36,f37
  f270: plane 18.4x1.72mm, normal (0,-1,0), area 8.5mm2, adj f16,f17,f18,f27,f28,f29,f30,f31
  f271: plane 106.65x7.77mm, normal (-1,0,0), area 829mm2, adj f97,f193,f264,f265
  f272: plane 106.65x7.77mm, normal (1,0,0), area 829mm2, adj f97,f192,f264,f265
PLACE A at identity
PLACE B t=(0,2.54,0)mm
MATE fastened B.f6 <-> A.f26  axis (0,-1,0) through (0,2.54,0)mm
